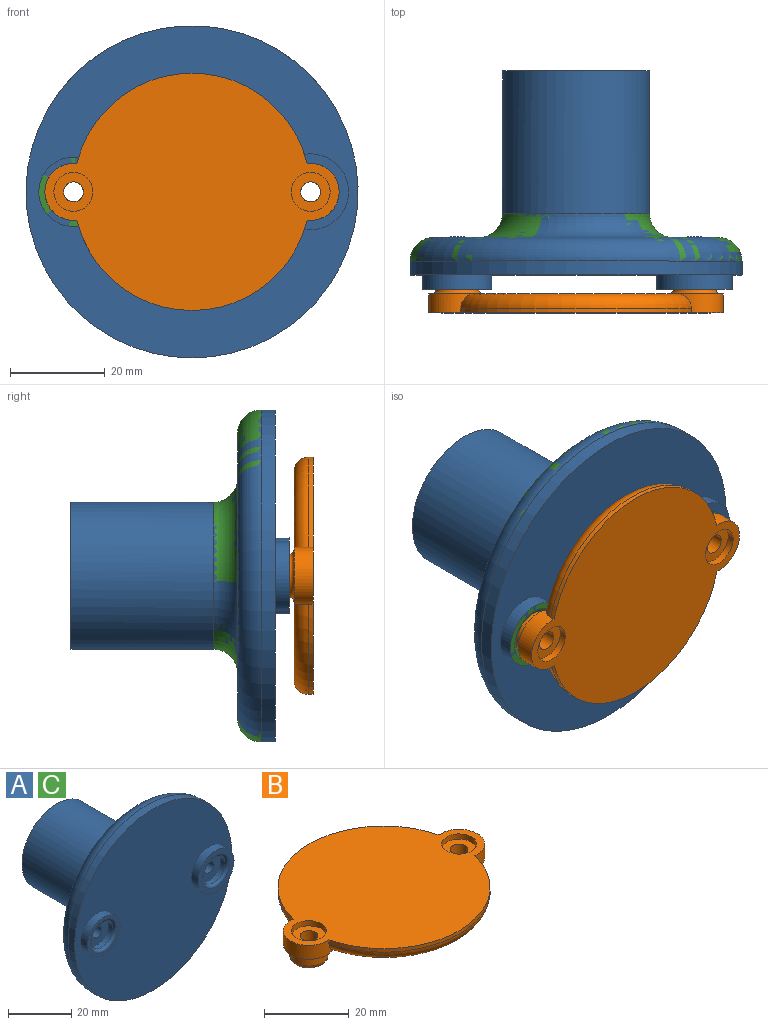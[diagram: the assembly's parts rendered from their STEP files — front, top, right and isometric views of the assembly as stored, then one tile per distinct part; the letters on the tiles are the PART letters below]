
ASSEMBLY  parts=3 mates=1
PART A: 48 faces, bbox 76.3x46.6x76.3 mm
  f0: plane 60x30mm, normal (0,1,0), area 676.4mm2, adj f23,f31,f46,f47
  f1: cylinder r=35mm len=70mm, axis (0,1,0), area 637.7mm2, adj f2,f46
  f2: plane 70x70mm, normal (0,-1,0), area 3480.9mm2, adj f1,f4,f8
  f3: cylinder r=5mm len=10mm, axis (0,1,0), area 62.8mm2, adj f6,f12
  f4: cylinder r=7.28mm len=14.56mm, axis (0,1,0), area 137.2mm2, adj f2,f5
  f5: plane 14.56x14.56mm, normal (0,-1,0), area 53.4mm2, adj f4,f12
  f6: plane 10x10mm, normal (0,-1,0), area 64.7mm2, adj f3,f14
  f7: cylinder r=5mm len=10mm, axis (0,1,0), area 62.8mm2, adj f10,f11
  f8: cylinder r=8mm len=16mm, axis (0,1,0), area 150.8mm2, adj f2,f9
  f9: plane 16x16mm, normal (0,-1,0), area 88mm2, adj f8,f11
  f10: plane 10x10mm, normal (0,-1,0), area 64.7mm2, adj f7,f13
  f11: torus R=6mm, axis (0,-1,0), area 52.9mm2, adj f7,f9
  f12: torus R=6mm, axis (0,-1,0), area 52.9mm2, adj f3,f5
  f13: cylinder r=2.1mm len=4.9mm, axis (0,1,0), area 64.7mm2, adj f10,f45
  f14: cylinder r=2.1mm len=4.9mm, axis (0,1,0), area 64.7mm2, adj f6,f44
  f15: plane 60x30mm, normal (0,1,0), area 676.4mm2, adj f23,f31,f46,f47
  f16: plane 3.6x3.1mm, normal (-0.87,0,-0.5), area 12.9mm2, adj f17,f21,f22,f44
  f17: plane 3.6x3.1mm, normal (-0.87,0,0.5), area 12.9mm2, adj f16,f18,f22,f44
  f18: plane 4.16x3.1mm, normal (0,0,1), area 12.9mm2, adj f17,f19,f22,f44
  f19: plane 3.6x3.1mm, normal (0.87,0,0.5), area 12.9mm2, adj f18,f20,f22,f44
  f20: plane 3.6x3.1mm, normal (0.87,0,-0.5), area 12.9mm2, adj f19,f21,f22,f44
  f21: plane 4.16x3.1mm, normal (0,0,-1), area 12.9mm2, adj f16,f20,f22,f44
  f22: plane 10x10mm, normal (0,1,0), area 33.6mm2, adj f16,f17,f18,f19,f20,f21,f23
  f23: cylinder r=5mm len=10mm, axis (0,-1,0), area 3.1mm2, adj f0,f15,f22,f47
  f24: plane 3.55x3.1mm, normal (-0.86,0,-0.51), area 12.8mm2, adj f25,f29,f30,f45
  f25: plane 3.6x3.1mm, normal (-0.87,0,0.49), area 12.8mm2, adj f24,f26,f30,f45
  f26: plane 4.13x3.1mm, normal (-0.01,0,1), area 12.8mm2, adj f25,f27,f30,f45
  f27: plane 3.55x3.1mm, normal (0.86,0,0.51), area 12.8mm2, adj f26,f28,f30,f45
  f28: plane 3.6x3.1mm, normal (0.87,0,-0.49), area 12.8mm2, adj f27,f29,f30,f45
  f29: plane 4.13x3.1mm, normal (0.01,0,-1), area 12.8mm2, adj f24,f28,f30,f45
  f30: plane 10x10mm, normal (0,1,0), area 34.3mm2, adj f24,f25,f26,f27,f28,f29,f31
  f31: cylinder r=5mm len=10mm, axis (0,-1,0), area 3.1mm2, adj f0,f15,f30,f47
  f32: plane 28.56x24.92mm, normal (0,1,0), area 81.5mm2, adj f33,f34,f35,f36
  f33: bspline ~32.33x28mm, area 723.9mm2, adj f32,f35,f36,f37,f38,f39,f40,f43
  f34: bspline ~32.33x28mm, area 723.9mm2, adj f32,f35,f36,f37,f38,f39,f40,f43
  f35: cylinder r=12mm len=24mm, axis (0,1,0), area 470.6mm2, adj f32,f33,f34,f43
  f36: cylinder r=14mm len=28mm, axis (0,1,0), area 1689.8mm2, adj f32,f33,f34,f37,f41
  f37: cylinder r=14mm len=28mm, axis (0,1,0), area 130.4mm2, adj f33,f34,f36,f38
  f38: cylinder r=14mm len=28mm, axis (0,1,0), area 130.4mm2, adj f33,f34,f37,f39
  f39: cylinder r=14mm len=28mm, axis (0,1,0), area 130.5mm2, adj f33,f34,f38,f40
  f40: cylinder r=14mm len=28mm, axis (0,1,0), area 59.9mm2, adj f33,f34,f39,f43
  f41: plane 31x31mm, normal (0,1,0), area 139mm2, adj f36,f42
  f42: cylinder r=15.5mm len=31mm, axis (0,1,0), area 2931.4mm2, adj f41,f47
  f43: plane 26.54x26.54mm, normal (0,1,0), area 534.3mm2, adj f33,f34,f35,f40
  f44: plane 8.31x7.2mm, normal (0,1,0), area 31mm2, adj f14,f16,f17,f18,f19,f20,f21
  f45: plane 8.26x7.2mm, normal (0,1,0), area 30.4mm2, adj f13,f24,f25,f26,f27,f28,f29
  f46: torus R=30mm, axis (0,-1,0), area 1637.5mm2, adj f0,f1,f15
  f47: torus R=20.5mm, axis (0,-1,0), area 851.9mm2, adj f0,f15,f23,f31,f42
PART B: 22 faces, bbox 62.7x54.1x9.1 mm
  f0: cylinder r=6mm len=12mm, axis (0,0,-1), area 85.1mm2, adj f1,f3,f4,f5,f18,f19
  f1: cylinder r=25mm len=48.56mm, axis (0,0,-1), area 66.5mm2, adj f0,f2,f4,f19
  f2: cylinder r=6mm len=12mm, axis (0,0,-1), area 85.1mm2, adj f1,f3,f4,f5,f18,f19
  f3: cylinder r=25mm len=48.56mm, axis (0,0,-1), area 66.5mm2, adj f0,f2,f4,f18
  f4: plane 62x50mm, normal (0,0,1), area 1976.7mm2, adj f0,f1,f2,f3,f10,f12
  f5: plane 62x44mm, normal (0,0,-1), area 1516.3mm2, adj f0,f2,f16,f17,f18,f19
  f6: cylinder r=4.5mm len=9mm, axis (0,0,1), area 56.5mm2, adj f16,f21
  f7: plane 7x7mm, normal (0,0,-1), area 24.6mm2, adj f14,f21
  f8: cylinder r=4.5mm len=9mm, axis (0,0,1), area 56.5mm2, adj f17,f20
  f9: plane 7x7mm, normal (0,0,-1), area 24.6mm2, adj f15,f20
  f10: cylinder r=4.1mm len=8.2mm, axis (0,0,1), area 38.6mm2, adj f4,f11
  f11: plane 8.2x8.2mm, normal (0,0,1), area 39mm2, adj f10,f15
  f12: cylinder r=4.1mm len=8.2mm, axis (0,0,1), area 38.6mm2, adj f4,f13
  f13: plane 8.2x8.2mm, normal (0,0,1), area 39mm2, adj f12,f14
  f14: cylinder r=2.1mm len=6.5mm, axis (0,0,-1), area 85.8mm2, adj f7,f13
  f15: cylinder r=2.1mm len=6.5mm, axis (0,0,-1), area 85.8mm2, adj f9,f11
  f16: torus R=5.5mm, axis (0,0,1), area 48mm2, adj f5,f6
  f17: torus R=5.5mm, axis (0,0,1), area 48mm2, adj f5,f8
  f18: torus R=22mm, axis (0,0,1), area 300.1mm2, adj f0,f2,f3,f5
  f19: torus R=22mm, axis (0,0,1), area 300.1mm2, adj f0,f1,f2,f5
  f20: torus R=3.5mm, axis (0,0,-1), area 40.8mm2, adj f8,f9
  f21: torus R=3.5mm, axis (0,0,-1), area 40.8mm2, adj f6,f7
PART C: same geometry as A
PLACE A t=(-19.74,-1.76,6.95)mm
PLACE B rot(axis=(1,0,0),90deg) t=(-19.74,-30.76,6.95)mm
PLACE C t=(-19.74,-1.76,6.95)mm
MATE slider B.f15 <-> C.f7  axis (0,1,0) through (5.26,-26.76,6.95)mm
